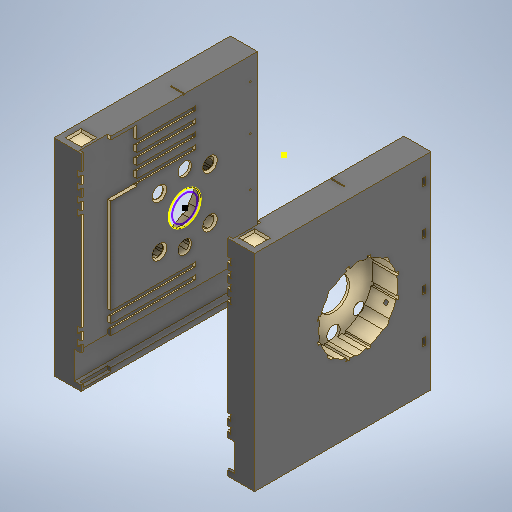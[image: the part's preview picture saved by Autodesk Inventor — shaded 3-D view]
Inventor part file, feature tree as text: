
AUTODESK INVENTOR PART (.ipt)
format: ipt  version: 2025.1 (Build 291241000, 241)  size: 2,158,080 bytes
history: native  units: mm
features: extrude x38, sketch x22, plane x2, chamfer x1, mirror x1
ambient origin geometry x8: Origin, YZ Plane, XZ Plane, XY Plane, X Axis, Y Axis, Z Axis, Center Point
bodies: Volumenkörper1 (feature_tree)
feature tree (64):
  extrude  "Extrusion1"  Depth=178.0mm
  extrude  "Extrusion2"  Depth=2.0mm
  extrude  "Extrusion3"  Depth=17.0mm
  extrude  "Extrusion4"  Depth=156.5mm TaperAngle=0.0deg
  extrude  "Extrusion5"  TaperAngle=45.0deg  [1 undecoded]
  extrude  "Extrusion6"  TaperAngle=45.0deg  [1 undecoded]
  extrude  "Extrusion7"  Depth=181.0mm TaperAngle=0.0deg
  extrude  "Extrusion8"  Depth=2.0mm TaperAngle=0.0deg
  plane  "Arbeitsebene1"
  extrude  "Extrusion9"  Depth=24.0mm
  extrude  "Extrusion10"  Depth=24.0mm
  extrude  "Extrusion11"  Depth=3.0mm TaperAngle=0.0deg
  extrude  "Extrusion12"  Depth=24.0mm
  extrude  "Extrusion13"  Depth=14.0mm
  extrude  "Extrusion14"  Depth=3.0mm TaperAngle=0.0deg
  extrude  "Extrusion15"  Depth=24.5mm
  extrude  "Extrusion16"  Depth=6.0mm
  extrude  "Extrusion17"  Depth=3.0mm TaperAngle=0.0deg
  extrude  "Extrusion20"  Depth=24.5mm
  extrude  "Extrusion21"  Depth=3.0mm
  extrude  "Extrusion22"  Depth=20.0mm
  extrude  "Extrusion23"  Depth=10.0mm
  extrude  "Extrusion24"  Depth=10.0mm
  extrude  "Extrusion25"  Depth=10.0mm
  extrude  "Extrusion26"  Depth=10.0mm
  extrude  "Extrusion27"  Depth=10.0mm
  extrude  "Extrusion28"  Depth=10.0mm
  plane  "Arbeitsebene2"
  extrude  "Extrusion29"  Depth=10.0mm
  extrude  "Extrusion30"  Depth=10.0mm
  extrude  "Extrusion31"  Depth=10.0mm
  extrude  "Extrusion32"  Depth=10.0mm
  extrude  "Extrusion33"  Depth=10.0mm
  extrude  "Extrusion34"  Depth=3.0mm
  sketch  "Skizze53"  dims[d46=6.0mm d47=6.0mm]
  extrude  "Extrusion38"  Depth=2.0mm
  chamfer  "Fasen2"  Distance=2.0mm
  extrude  "Extrusion39"  Depth=3.0mm TaperAngle=0.0deg
  extrude  "Extrusion40"  Depth=178.0mm
  extrude  "Extrusion42"  Depth=14.5mm
  extrude  "Extrusion43"  Depth=1.0mm
  sketch  "Skizze62"  dims[d61=10.0mm d62=10.0mm d63=10.0mm d64=10.0mm d65=10.0mm d66=10.0mm d67=10.0mm d68=10.0mm d69=10.0mm d70=10.0mm d71=10.0mm d75=8.0mm d76=2.0mm d77=2.0mm d78=114.0mm d79=0.0mm d80=178.0mm d81=14.5mm d82=1.0mm d83=1.0mm d84=154.0mm d85=154.0mm d86=1.0mm d87=0.0mm d88=1.0mm d89=0.0mm d90=130.0mm d91=130.0mm d94=1.0mm d98=3.0mm d99=0.0mm d100=3.0mm d101=0.0mm d102=3.0mm d103=0.0mm d105=92.5mm d106=110.2mm d107=15.0mm d108=15.0mm d109=15.0mm d110=15.0mm d112=3.4mm d113=3.4mm d114=3.4mm d115=3.4mm d116=3.4mm d117=3.4mm d118=3.4mm d119=0.0mm d120=0.0mm d121=0.0mm d122=0.0mm d123=0.0mm d125=0.0mm d126=0.0mm d127=0.0mm d128=0.0mm d129=0.0mm d130=0.0mm d131=3.4mm d132=120.7mm d133=103.0mm d134=2.5mm d140=24.0mm d141=24.0mm d142=24.0mm d143=24.0mm d144=24.0mm d145=24.0mm d146=24.0mm d147=5.0mm d148=0.0mm d161=5.0mm d162=5.0mm d163=5.0mm d164=5.0mm d165=5.0mm d166=5.0mm d167=5.0mm d168=5.0mm d169=14.0mm d170=14.0mm d171=14.0mm d172=14.0mm d173=14.0mm d174=14.0mm d175=14.0mm d176=14.0mm d177=3.0mm d178=0.0mm d179=20.0mm d180=2.0mm d181=2.0mm d182=1.0mm d183=0.0mm d184=20.0mm d185=0.0mm d186=130.0mm d187=14.0mm d188=6.0mm d189=6.0mm d190=6.0mm d191=6.0mm d192=6.0mm d193=6.0mm d194=6.0mm d195=6.0mm d196=20.0mm d197=0.0mm d198=24.0mm d199=0.0mm d200=24.0mm d201=0.0mm d202=12.0mm d203=0.0mm d204=3.0mm d205=0.0mm d206=-5.0mm d207=5.7mm d208=7.0mm d209=17.0mm d210=20.0mm d211=40.0mm d212=40.0mm d213=40.0mm d214=5.7mm d215=5.7mm d216=5.7mm d217=2.6mm d218=0.0mm d219=1.6mm d220=1.6mm d221=1.6mm d222=1.6mm d223=0.0mm d224=0.0mm d225=3.4mm d226=3.4mm d227=3.4mm d228=3.4mm d229=3.4mm d230=3.4mm d231=3.4mm d232=3.4mm d233=5.7mm d234=12.0mm d235=12.0mm d236=20.0mm d237=40.0mm d238=40.0mm d239=40.0mm d240=5.7mm d241=5.7mm d242=5.7mm d243=3.4mm d244=3.4mm d245=3.4mm d246=3.4mm d247=3.4mm d248=3.4mm d249=3.4mm d250=3.4mm d251=40.0mm d252=0.0mm d253=0.0mm d254=0.0mm d255=0.0mm d256=0.0mm d257=0.0mm d258=0.0mm d259=70.05mm d260=28.39mm d261=10.0mm d262=54.0mm d263=10.0mm d264=0.0mm d265=70.05mm d266=22.5mm d267=22.0mm d268=0.0mm d292=5.75mm d294=40.0mm d295=10.0mm d296=360.0deg d297=0.0mm d298=0.0mm d299=1.5mm d300=2.0mm d301=45.0deg d303=120.0mm d304=360.0deg d305=10.0mm d306=0.0mm d307=12.0mm d308=12.0mm d309=30.0mm d310=30.0mm d311=10.0mm d312=0.0mm d313=5.5mm d314=4.0mm d315=21.214477mm d316=5.5mm d317=4.0mm d318=5.5mm d319=4.0mm d320=5.5mm d321=4.0mm d322=5.5mm d323=4.0mm d324=5.5mm d325=4.0mm d326=5.5mm d327=4.0mm d328=5.5mm d329=4.0mm d330=5.5mm d331=4.0mm d332=5.5mm d333=4.0mm d334=5.5mm d335=4.0mm d336=5.5mm d337=4.0mm d338=5.5mm d339=4.0mm d341=5.5mm d342=4.0mm d347=3.0mm d348=23.0mm d349=50.0mm d350=0.0mm d351=3.0mm d352=0.0mm d353=24.0mm d354=24.0mm d355=14.0mm d356=14.0mm d357=3.0mm d358=0.0mm d359=0.5mm d360=0.872665mm]
  extrude  "Extrusion44"  Depth=1.0mm
  mirror  "Spiegeln2"
  sketch  "Skizze3"  dims[d0=183.0mm d1=178.0mm]
  sketch  "Skizze9"  dims[d7=24.0mm d8=156.5mm d9=0.0mm]
  sketch  "Skizze10"  dims[d10=5.0mm d11=45.0deg]
  sketch  "Skizze11"  dims[d12=45.0deg d13=45.0deg]
  sketch  "Skizze12"  dims[d14=45.0deg d15=181.0mm d16=0.0mm]
  sketch  "Skizze14"  dims[d17=5.0mm d18=0.0mm d19=2.0mm d20=0.0mm]
  sketch  "Skizze30"  dims[d21=5.0mm d22=24.0mm]
  sketch  "Skizze36"  dims[d23=24.0mm d24=150.7mm]
  sketch  "Skizze45"  dims[d25=133.0mm d26=3.0mm d27=0.0mm]
  sketch  "Skizze46"  dims[d36=0.0mm d37=0.0mm d38=24.0mm]
  sketch  "Skizze47"  dims[d39=24.0mm d40=14.0mm]
  sketch  "Skizze48"  dims[d41=14.0mm d42=3.0mm d43=0.0mm]
  sketch  "Skizze49"  dims[d44=5.0mm d45=24.5mm]
  sketch  "Skizze54"  dims[d48=3.0mm d49=0.0mm d50=3.0mm d51=0.0mm]
  sketch  "Skizze - Runde Anordnung3"  dims[d2=24.0mm d3=0.0mm d4=2.0mm]
  sketch  "Skizze55"  dims[d52=2.0mm d53=24.5mm]
  sketch  "Skizze - Runde Anordnung4"  dims[d5=2.0mm d6=17.0mm]
  sketch  "Skizze56"  dims[d54=3.0mm d55=3.0mm]
  sketch  "Skizze60"  dims[d56=181.0mm d57=0.0mm d58=20.0mm]
  sketch  "Skizze61"  dims[d59=10.0mm d60=10.0mm]
note: 2 required parameter values undecoded (feature->parameter linkage not recoverable at this tier; creation-order binding heuristic only, values carry confidence <= 0.55)
